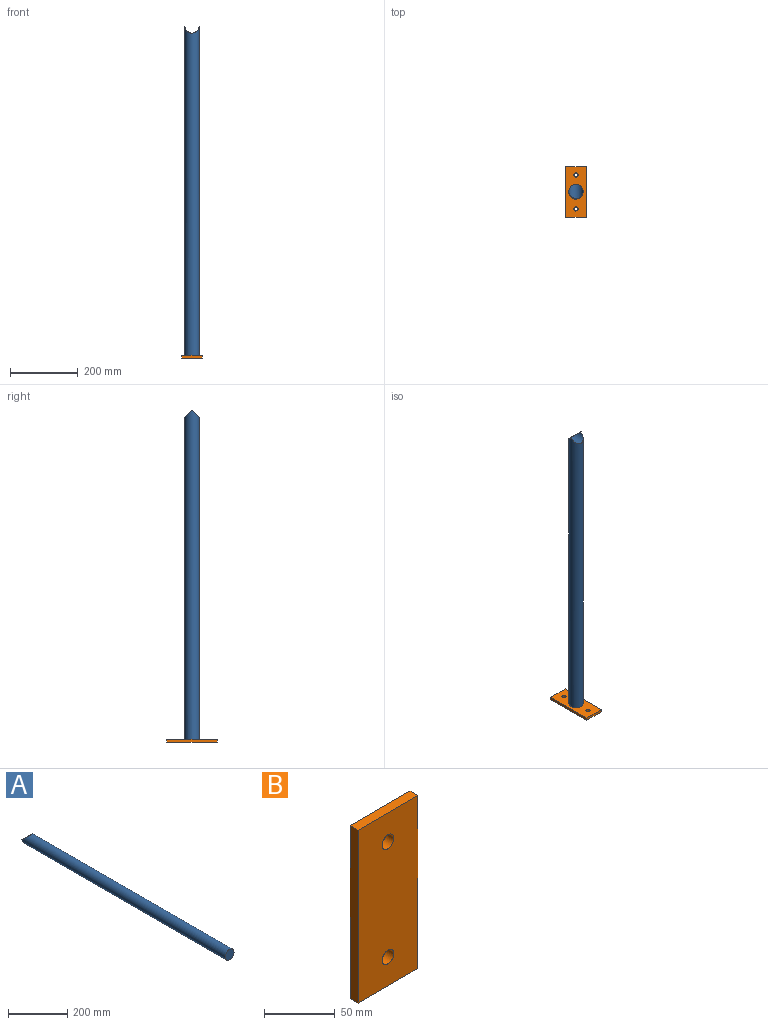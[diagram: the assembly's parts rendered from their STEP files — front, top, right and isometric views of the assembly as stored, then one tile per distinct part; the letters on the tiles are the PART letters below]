
ASSEMBLY  parts=2 mates=1
PART A: 3 faces, bbox 42x970x42.1 mm
  f0: cylinder r=21mm len=970mm, axis (0,1,0), area 126224.5mm2, adj f1,f2
  f1: plane 42x42mm, normal (0,-1,0), area 1385.4mm2, adj f0
  f2: cylinder r=21mm len=42.14mm, axis (0,0,1), area 1764mm2, adj f0
PART B: 8 faces, bbox 60x8x150 mm
  f0: plane 60x8mm, normal (0,0,-1), area 480mm2, adj f1,f5,f6,f7
  f1: plane 150x8mm, normal (1,0,0), area 1200mm2, adj f0,f2,f6,f7
  f2: plane 60x8mm, normal (0,0,1), area 480mm2, adj f1,f5,f6,f7
  f3: cylinder r=6mm len=12mm, axis (0,1,0), area 301.6mm2, adj f6,f7
  f4: cylinder r=6mm len=12mm, axis (0,1,0), area 301.6mm2, adj f6,f7
  f5: plane 150x8mm, normal (-1,0,0), area 1200mm2, adj f0,f2,f6,f7
  f6: plane 150x60mm, normal (0,-1,0), area 8773.8mm2, adj f0,f1,f2,f3,f4,f5
  f7: plane 150x60mm, normal (0,1,0), area 8773.8mm2, adj f0,f1,f2,f3,f4,f5
PLACE A rot(axis=(1,0,0),90deg) t=(26.28,-530.41,541.95)mm
PLACE B rot(axis=(-1,0,0),90deg) t=(26.28,-530.41,-432.05)mm
MATE fastened A.f0 <-> B.f6  axis (0,0,-1) through (26.28,-530.41,-428.05)mm
